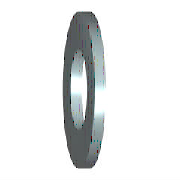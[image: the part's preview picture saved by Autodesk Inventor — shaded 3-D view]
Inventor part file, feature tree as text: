
AUTODESK INVENTOR PART (.ipt)
format: ipt  version: 2020.1 (Build 241239000, 239)  size: 110,080 bytes
history: native  units: mm (DEFAULTED — no unit token found)
features: other x1, plane x1, sketch x1
ambient origin geometry x7: Origin, YZ Plane, XY Plane, X Axis, Y Axis, Z Axis, Center Point
bodies: Solid1 (feature_tree), Body (feature_tree)
feature tree (3):
  other  "Work Axis1"
  plane  "Work Plane1"
  sketch  "Sketch"  dims[d0=3.2mm d1=6.0mm d2=0.5mm d3=0.0mm d4=0.0mm d5=0.0mm d6=0.0mm d7=0.0mm]
